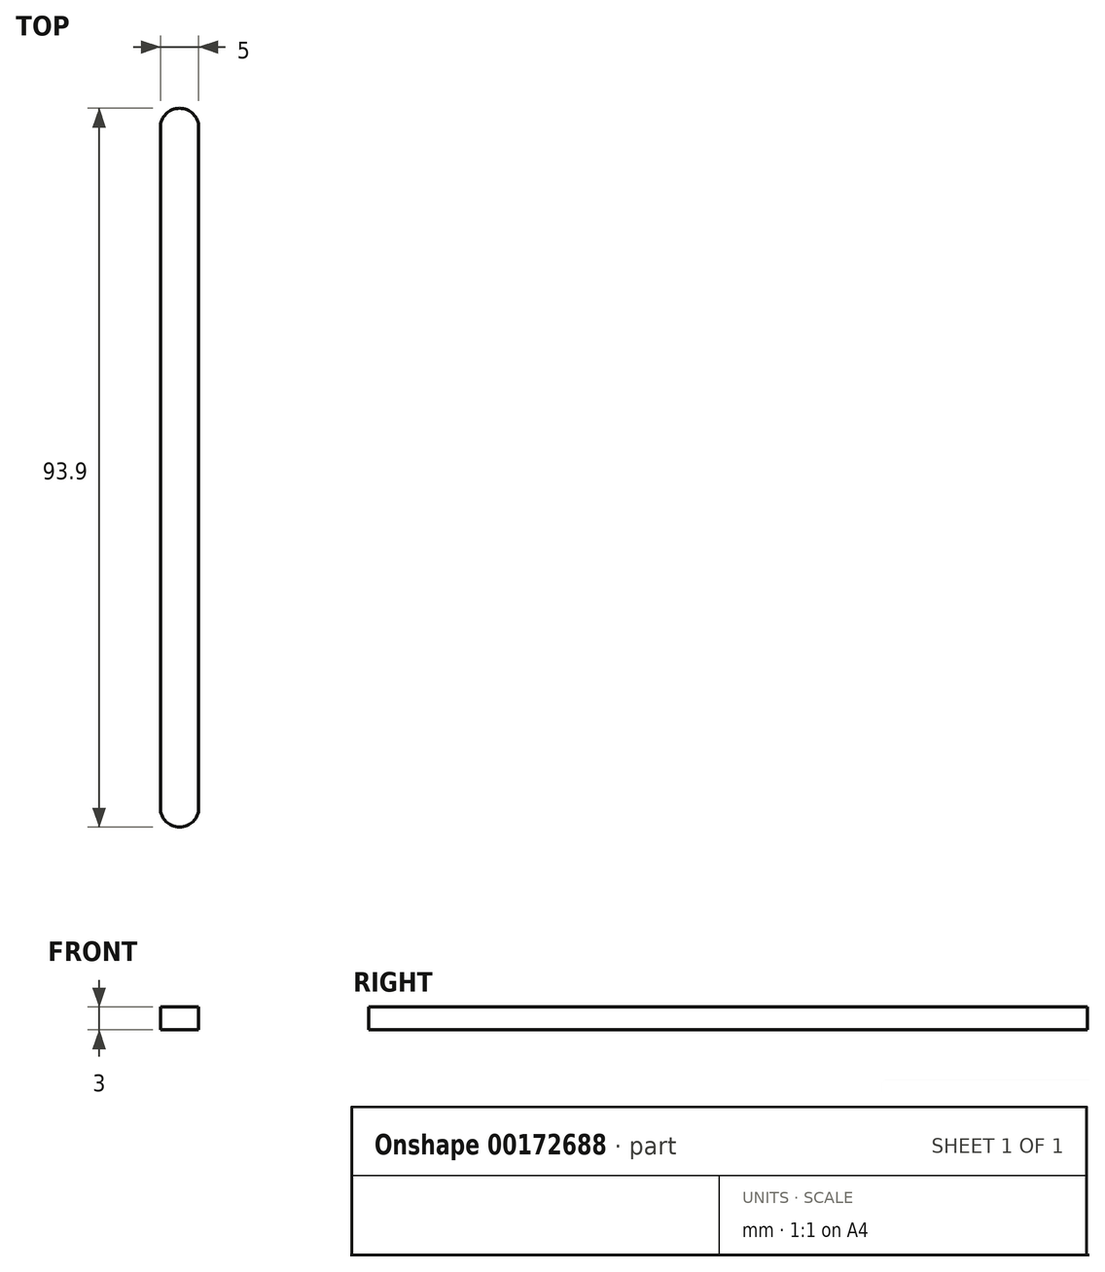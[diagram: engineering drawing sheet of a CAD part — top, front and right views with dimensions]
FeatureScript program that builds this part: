
annotation { "Feature Type Name" : "Feature", "Feature Type Description" : "" }
export const myFeature = defineFeature(function(context is Context, id is Id, definition is map)
    precondition{}
    {
        {
            var Q0;
            Q0=qCreatedBy(makeId("Top.planeOp"),FACE);
            var sketch = newSketch(context, id + "F0", { "sketchPlane" : qUnion([Q0])});
            skLineSegment(sketch, "E0", {"start": v(-1.75, 67.98) * mm, "end": v(-1.75, -46.32) * mm});
            skLineSegment(sketch, "E1", {"start": v(-22.75, 67.98) * mm, "end": v(-22.75, -20.92) * mm});
            skLineSegment(sketch, "E2", {"start": v(-104.51, -51.12) * mm, "end": v(-35.45, -18.92) * mm});
            skLineSegment(sketch, "E3", {"start": v(-91.81, -68.37) * mm, "end": v(-22.75, -36.16) * mm});
            skLineSegment(sketch, "E4", {"start": v(-99.28, -84.88) * mm, "end": v(50.8, -58.42) * mm});
            skArc(sketch, "E5.4.startCap", {"start": v(-25.25, 67.98) * mm, "mid": v(-22.75, 70.48) * mm, "end": v(-20.25, 67.98) * mm});
            skArc(sketch, "E5.4.endCap", {"start": v(-20.25, -20.92) * mm, "mid": v(-22.75, -23.42) * mm, "end": v(-25.25, -20.92) * mm});
            skLineSegment(sketch, "E5.4.left", {"start": v(-20.25, 67.98) * mm, "end": v(-20.25, -20.92) * mm});
            skLineSegment(sketch, "E5.4.right", {"start": v(-25.25, 67.98) * mm, "end": v(-25.25, -20.92) * mm});
            skArc(sketch, "E5.5.startCap", {"start": v(-103.46, -53.39) * mm, "mid": v(-106.78, -52.18) * mm, "end": v(-105.57, -48.85) * mm});
            skArc(sketch, "E5.5.endCap", {"start": v(-36.5, -16.65) * mm, "mid": v(-33.19, -17.86) * mm, "end": v(-34.4, -21.18) * mm});
            skLineSegment(sketch, "E5.5.left", {"start": v(-105.57, -48.85) * mm, "end": v(-36.5, -16.65) * mm});
            skLineSegment(sketch, "E5.5.right", {"start": v(-103.46, -53.39) * mm, "end": v(-34.4, -21.18) * mm});
            skArc(sketch, "E5.6.startCap", {"start": v(-90.76, -70.63) * mm, "mid": v(-94.08, -69.42) * mm, "end": v(-92.87, -66.1) * mm});
            skArc(sketch, "E5.6.endCap", {"start": v(-23.8, -33.9) * mm, "mid": v(-20.49, -35.1) * mm, "end": v(-21.7, -38.43) * mm});
            skLineSegment(sketch, "E5.6.left", {"start": v(-92.87, -66.1) * mm, "end": v(-23.8, -33.9) * mm});
            skLineSegment(sketch, "E5.6.right", {"start": v(-90.76, -70.63) * mm, "end": v(-21.7, -38.43) * mm});
            skArc(sketch, "E5.7.startCap", {"start": v(-98.85, -87.35) * mm, "mid": v(-101.75, -85.32) * mm, "end": v(-99.72, -82.42) * mm});
            skArc(sketch, "E5.7.endCap", {"start": v(50.37, -55.96) * mm, "mid": v(53.26, -57.99) * mm, "end": v(51.23, -60.88) * mm});
            skLineSegment(sketch, "E5.7.left", {"start": v(-99.72, -82.42) * mm, "end": v(50.37, -55.96) * mm});
            skLineSegment(sketch, "E5.7.right", {"start": v(-98.85, -87.35) * mm, "end": v(51.23, -60.88) * mm});
            skLineSegment(sketch, "E6", {"start": v(-25.75, 75.98) * mm, "end": v(84.75, 75.98) * mm});
            skLineSegment(sketch, "E7", {"start": v(86.14, -60.31) * mm, "end": v(-100.85, -93.28) * mm});
            skLineSegment(sketch, "E8", {"start": v(-106.64, -89.23) * mm, "end": v(-113.28, -51.57) * mm});
            skLineSegment(sketch, "E9", {"start": v(-109.71, -44.72) * mm, "end": v(-45.42, -14.74) * mm});
            skLineSegment(sketch, "E10", {"start": v(-30.75, 8.28) * mm, "end": v(-30.75, 70.98) * mm});
            skPoint(sketch, "E11.visualSharp", {"position": v(-30.75, -7.9) * mm});
            skArc(sketch, "E11.filletArc", {"start": v(-45.42, -14.74) * mm, "mid": v(-34.73, -5.36) * mm, "end": v(-30.75, 8.28) * mm});
            skPoint(sketch, "E12.visualSharp", {"position": v(-108.55, -78.4) * mm});
            skPoint(sketch, "E13.visualSharp", {"position": v(-105.77, -94.15) * mm});
            skArc(sketch, "E13.filletArc", {"start": v(-106.64, -89.23) * mm, "mid": v(-104.59, -92.46) * mm, "end": v(-100.85, -93.28) * mm});
            skPoint(sketch, "E14.visualSharp", {"position": v(-30.75, 75.98) * mm});
            skArc(sketch, "E14.filletArc", {"start": v(-25.75, 75.98) * mm, "mid": v(-29.29, 74.51) * mm, "end": v(-30.75, 70.98) * mm});
            skArc(sketch, "E15.0.startCap", {"start": v(-4.25, 67.98) * mm, "mid": v(-1.75, 70.48) * mm, "end": v(0.75, 67.98) * mm});
            skArc(sketch, "E15.0.endCap", {"start": v(0.75, -46.32) * mm, "mid": v(-1.75, -48.82) * mm, "end": v(-4.25, -46.32) * mm});
            skLineSegment(sketch, "E15.0.left", {"start": v(0.75, 67.98) * mm, "end": v(0.75, -46.32) * mm});
            skLineSegment(sketch, "E15.0.right", {"start": v(-4.25, 67.98) * mm, "end": v(-4.25, -46.32) * mm});
            skLineSegment(sketch, "E16.1.0.0", {"start": v(16.75, 67.98) * mm, "end": v(16.75, -46.32) * mm});
            skLineSegment(sketch, "E16.1.0.1", {"start": v(19.25, 67.98) * mm, "end": v(19.25, -46.32) * mm});
            skLineSegment(sketch, "E16.1.0.2", {"start": v(21.75, 67.98) * mm, "end": v(21.75, -46.32) * mm});
            skArc(sketch, "E16.1.0.3", {"start": v(16.75, 67.98) * mm, "mid": v(19.25, 70.48) * mm, "end": v(21.75, 67.98) * mm});
            skArc(sketch, "E16.1.0.4", {"start": v(21.75, -46.32) * mm, "mid": v(19.25, -48.82) * mm, "end": v(16.75, -46.32) * mm});
            skLineSegment(sketch, "E16.2.0.0", {"start": v(37.75, 67.98) * mm, "end": v(37.75, -46.32) * mm});
            skLineSegment(sketch, "E16.2.0.1", {"start": v(40.25, 67.98) * mm, "end": v(40.25, -46.32) * mm});
            skLineSegment(sketch, "E16.2.0.2", {"start": v(42.75, 67.98) * mm, "end": v(42.75, -46.32) * mm});
            skArc(sketch, "E16.2.0.3", {"start": v(37.75, 67.98) * mm, "mid": v(40.25, 70.48) * mm, "end": v(42.75, 67.98) * mm});
            skArc(sketch, "E16.2.0.4", {"start": v(42.75, -46.32) * mm, "mid": v(40.25, -48.82) * mm, "end": v(37.75, -46.32) * mm});
            skLineSegment(sketch, "E16.3.0.0", {"start": v(58.75, 67.98) * mm, "end": v(58.75, -46.32) * mm});
            skLineSegment(sketch, "E16.3.0.1", {"start": v(61.25, 67.98) * mm, "end": v(61.25, -46.32) * mm});
            skLineSegment(sketch, "E16.3.0.2", {"start": v(63.75, 67.98) * mm, "end": v(63.75, -46.32) * mm});
            skArc(sketch, "E16.3.0.3", {"start": v(58.75, 67.98) * mm, "mid": v(61.25, 70.48) * mm, "end": v(63.75, 67.98) * mm});
            skArc(sketch, "E16.3.0.4", {"start": v(63.75, -46.32) * mm, "mid": v(61.25, -48.82) * mm, "end": v(58.75, -46.32) * mm});
            skLineSegment(sketch, "E16.4.0.0", {"start": v(79.75, 67.98) * mm, "end": v(79.75, -46.32) * mm});
            skLineSegment(sketch, "E16.4.0.1", {"start": v(82.25, 67.98) * mm, "end": v(82.25, -46.32) * mm});
            skLineSegment(sketch, "E16.4.0.2", {"start": v(84.75, 67.98) * mm, "end": v(84.75, -46.32) * mm});
            skArc(sketch, "E16.4.0.3", {"start": v(79.75, 67.98) * mm, "mid": v(82.25, 70.48) * mm, "end": v(84.75, 67.98) * mm});
            skArc(sketch, "E16.4.0.4", {"start": v(84.75, -46.32) * mm, "mid": v(82.25, -48.82) * mm, "end": v(79.75, -46.32) * mm});
            skLineSegment(sketch, "E16.direction1", {"start": v(-4.25, -46.32) * mm, "end": v(16.75, -46.32) * mm, "construction": true});
            skLineSegment(sketch, "E17", {"start": v(92.75, -52.43) * mm, "end": v(92.75, 67.98) * mm});
            skArc(sketch, "E18.filletArc", {"start": v(92.75, 67.98) * mm, "mid": v(90.4, 73.63) * mm, "end": v(84.75, 75.98) * mm});
            skPoint(sketch, "E19.visualSharp", {"position": v(92.75, -59.15) * mm});
            skArc(sketch, "E19.filletArc", {"start": v(86.14, -60.31) * mm, "mid": v(90.88, -57.58) * mm, "end": v(92.75, -52.43) * mm});
            skPoint(sketch, "E20.visualSharp", {"position": v(-114.13, -46.78) * mm});
            skArc(sketch, "E20.filletArc", {"start": v(-109.71, -44.72) * mm, "mid": v(-112.66, -47.54) * mm, "end": v(-113.28, -51.57) * mm});
            skSolve(sketch);
        }
        {
            var Q0;
            Q0=makeQuery(id+"F0.imprint","IMPRINT",FACE,{"disambiguationData":[TD([[makeQuery(id+"F0.imprint","IMPRINT",EDGE,{"derivedFrom":sQuery(id+"F0.wireOp",EDGE,"E5.4.startCap")}),1.0]])]});
            extrude(context, id + "F1", {"entities" : qUnion([Q0]), "depth" : 6 * mm});
        }
        {
            var Q0;
            Q0=makeQuery(id+"F1.opExtrude","CAP_FACE",FACE,{"disambiguationData":[OSD([sQuery(id+"F0.wireOp",EDGE,"E5.4.startCap"),sQuery(id+"F0.wireOp",EDGE,"E5.4.endCap"),sQuery(id+"F0.wireOp",EDGE,"E5.4.left"),sQuery(id+"F0.wireOp",EDGE,"E5.4.right"),sQuery(id+"F0.wireOp",EDGE,"E5.5.startCap"),sQuery(id+"F0.wireOp",EDGE,"E5.5.endCap"),sQuery(id+"F0.wireOp",EDGE,"E5.5.left"),sQuery(id+"F0.wireOp",EDGE,"E5.5.right"),sQuery(id+"F0.wireOp",EDGE,"E5.6.startCap"),sQuery(id+"F0.wireOp",EDGE,"E5.6.endCap"),sQuery(id+"F0.wireOp",EDGE,"E5.6.left"),sQuery(id+"F0.wireOp",EDGE,"E5.6.right"),sQuery(id+"F0.wireOp",EDGE,"E5.7.startCap"),sQuery(id+"F0.wireOp",EDGE,"E5.7.endCap"),sQuery(id+"F0.wireOp",EDGE,"E5.7.left"),sQuery(id+"F0.wireOp",EDGE,"E5.7.right"),sQuery(id+"F0.wireOp",EDGE,"E6"),sQuery(id+"F0.wireOp",EDGE,"E7"),sQuery(id+"F0.wireOp",EDGE,"E8"),sQuery(id+"F0.wireOp",EDGE,"ev5cbhRx-Xfhe-EjYM-3IOK-P7PErRR7EIuT"),sQuery(id+"F0.wireOp",EDGE,"4vSNfU6F-C1qH-3bgV-W2vF-ly2UdOvPPW9B"),sQuery(id+"F0.wireOp",EDGE,"E9"),sQuery(id+"F0.wireOp",EDGE,"E10"),sQuery(id+"F0.wireOp",EDGE,"07c6aec0-4847-45df-b5d5-83fb8df157c1.filletArc"),sQuery(id+"F0.wireOp",EDGE,"6f2fbac6-5da2-46ef-aa15-745e75e4c3b5.filletArc"),sQuery(id+"F0.wireOp",EDGE,"E11.filletArc"),sQuery(id+"F0.wireOp",EDGE,"E12.filletArc"),sQuery(id+"F0.wireOp",EDGE,"E13.filletArc"),sQuery(id+"F0.wireOp",EDGE,"E14.filletArc"),sQuery(id+"F0.wireOp",EDGE,"E15.0.startCap"),sQuery(id+"F0.wireOp",EDGE,"E15.0.endCap"),sQuery(id+"F0.wireOp",EDGE,"E15.0.left"),sQuery(id+"F0.wireOp",EDGE,"E15.0.right"),sQuery(id+"F0.wireOp",EDGE,"E16.1.0.0"),sQuery(id+"F0.wireOp",EDGE,"E16.1.0.2"),sQuery(id+"F0.wireOp",EDGE,"E16.1.0.3"),sQuery(id+"F0.wireOp",EDGE,"E16.1.0.4"),sQuery(id+"F0.wireOp",EDGE,"E16.2.0.0"),sQuery(id+"F0.wireOp",EDGE,"E16.2.0.2"),sQuery(id+"F0.wireOp",EDGE,"E16.2.0.3"),sQuery(id+"F0.wireOp",EDGE,"E16.2.0.4"),sQuery(id+"F0.wireOp",EDGE,"E16.3.0.0"),sQuery(id+"F0.wireOp",EDGE,"E16.3.0.2"),sQuery(id+"F0.wireOp",EDGE,"E16.3.0.3"),sQuery(id+"F0.wireOp",EDGE,"E16.3.0.4"),sQuery(id+"F0.wireOp",EDGE,"E16.4.0.0"),sQuery(id+"F0.wireOp",EDGE,"E16.4.0.2"),sQuery(id+"F0.wireOp",EDGE,"E16.4.0.3"),sQuery(id+"F0.wireOp",EDGE,"E16.4.0.4"),sQuery(id+"F0.wireOp",EDGE,"E17"),sQuery(id+"F0.wireOp",EDGE,"E18.filletArc"),sQuery(id+"F0.wireOp",EDGE,"E19.filletArc")])],"isStart":true});
            var sketch = newSketch(context, id + "F2", { "sketchPlane" : qUnion([Q0])});
            skLineSegment(sketch, "E21", {"start": v(82.25, 46.32) * mm, "end": v(82.25, -67.98) * mm});
            skLineSegment(sketch, "E22", {"start": v(61.25, 46.32) * mm, "end": v(61.25, -67.98) * mm});
            skLineSegment(sketch, "E23", {"start": v(40.25, 46.32) * mm, "end": v(40.25, -67.98) * mm});
            skLineSegment(sketch, "E24", {"start": v(19.25, 46.32) * mm, "end": v(19.25, -67.98) * mm});
            skLineSegment(sketch, "E25", {"start": v(-1.75, 46.32) * mm, "end": v(-1.75, -67.98) * mm});
            skLineSegment(sketch, "E26", {"start": v(-22.75, 20.92) * mm, "end": v(-22.75, -67.98) * mm});
            skLineSegment(sketch, "E27", {"start": v(-35.45, 18.92) * mm, "end": v(-104.51, 51.12) * mm});
            skLineSegment(sketch, "E28", {"start": v(-22.75, 36.16) * mm, "end": v(-91.81, 68.37) * mm});
            skLineSegment(sketch, "E29", {"start": v(50.8, 58.42) * mm, "end": v(-99.28, 84.88) * mm});
            skArc(sketch, "E30.0.startCap", {"start": v(77.25, 46.32) * mm, "mid": v(82.25, 51.32) * mm, "end": v(87.25, 46.32) * mm});
            skArc(sketch, "E30.0.endCap", {"start": v(87.25, -67.98) * mm, "mid": v(82.25, -72.98) * mm, "end": v(77.25, -67.98) * mm});
            skLineSegment(sketch, "E30.0.left", {"start": v(87.25, 46.32) * mm, "end": v(87.25, -67.98) * mm});
            skLineSegment(sketch, "E30.0.right", {"start": v(77.25, 46.32) * mm, "end": v(77.25, -67.98) * mm});
            skArc(sketch, "E30.1.startCap", {"start": v(56.25, 46.32) * mm, "mid": v(61.25, 51.32) * mm, "end": v(66.25, 46.32) * mm});
            skArc(sketch, "E30.1.endCap", {"start": v(66.25, -67.98) * mm, "mid": v(61.25, -72.98) * mm, "end": v(56.25, -67.98) * mm});
            skLineSegment(sketch, "E30.1.left", {"start": v(66.25, 46.32) * mm, "end": v(66.25, -67.98) * mm});
            skLineSegment(sketch, "E30.1.right", {"start": v(56.25, 46.32) * mm, "end": v(56.25, -67.98) * mm});
            skArc(sketch, "E30.2.startCap", {"start": v(35.25, 46.32) * mm, "mid": v(40.25, 51.32) * mm, "end": v(45.25, 46.32) * mm});
            skArc(sketch, "E30.2.endCap", {"start": v(45.25, -67.98) * mm, "mid": v(40.25, -72.98) * mm, "end": v(35.25, -67.98) * mm});
            skLineSegment(sketch, "E30.2.left", {"start": v(45.25, 46.32) * mm, "end": v(45.25, -67.98) * mm});
            skLineSegment(sketch, "E30.2.right", {"start": v(35.25, 46.32) * mm, "end": v(35.25, -67.98) * mm});
            skArc(sketch, "E30.3.startCap", {"start": v(14.25, 46.32) * mm, "mid": v(19.25, 51.32) * mm, "end": v(24.25, 46.32) * mm});
            skArc(sketch, "E30.3.endCap", {"start": v(24.25, -67.98) * mm, "mid": v(19.25, -72.98) * mm, "end": v(14.25, -67.98) * mm});
            skLineSegment(sketch, "E30.3.left", {"start": v(24.25, 46.32) * mm, "end": v(24.25, -67.98) * mm});
            skLineSegment(sketch, "E30.3.right", {"start": v(14.25, 46.32) * mm, "end": v(14.25, -67.98) * mm});
            skArc(sketch, "E30.4.startCap", {"start": v(-6.75, 46.32) * mm, "mid": v(-1.75, 51.32) * mm, "end": v(3.25, 46.32) * mm});
            skArc(sketch, "E30.4.endCap", {"start": v(3.25, -67.98) * mm, "mid": v(-1.75, -72.98) * mm, "end": v(-6.75, -67.98) * mm});
            skLineSegment(sketch, "E30.4.left", {"start": v(3.25, 46.32) * mm, "end": v(3.25, -67.98) * mm});
            skLineSegment(sketch, "E30.4.right", {"start": v(-6.75, 46.32) * mm, "end": v(-6.75, -67.98) * mm});
            skArc(sketch, "E30.5.startCap", {"start": v(-20.64, 40.7) * mm, "mid": v(-18.22, 34.05) * mm, "end": v(-24.86, 31.63) * mm});
            skArc(sketch, "E30.5.endCap", {"start": v(-93.92, 63.84) * mm, "mid": v(-96.34, 70.48) * mm, "end": v(-89.7, 72.9) * mm});
            skLineSegment(sketch, "E30.5.left", {"start": v(-24.86, 31.63) * mm, "end": v(-93.92, 63.84) * mm});
            skLineSegment(sketch, "E30.5.right", {"start": v(-20.64, 40.7) * mm, "end": v(-89.7, 72.9) * mm});
            skArc(sketch, "E30.6.startCap", {"start": v(-27.75, 20.92) * mm, "mid": v(-22.75, 25.92) * mm, "end": v(-17.75, 20.92) * mm});
            skArc(sketch, "E30.6.endCap", {"start": v(-17.75, -67.98) * mm, "mid": v(-22.75, -72.98) * mm, "end": v(-27.75, -67.98) * mm});
            skLineSegment(sketch, "E30.6.left", {"start": v(-17.75, 20.92) * mm, "end": v(-17.75, -67.98) * mm});
            skLineSegment(sketch, "E30.6.right", {"start": v(-27.75, 20.92) * mm, "end": v(-27.75, -67.98) * mm});
            skArc(sketch, "E30.7.startCap", {"start": v(-33.34, 23.45) * mm, "mid": v(-30.92, 16.8) * mm, "end": v(-37.56, 14.38) * mm});
            skArc(sketch, "E30.7.endCap", {"start": v(-106.62, 46.59) * mm, "mid": v(-109.04, 53.23) * mm, "end": v(-102.4, 55.65) * mm});
            skLineSegment(sketch, "E30.7.left", {"start": v(-37.56, 14.38) * mm, "end": v(-106.62, 46.59) * mm});
            skLineSegment(sketch, "E30.7.right", {"start": v(-33.34, 23.45) * mm, "end": v(-102.4, 55.65) * mm});
            skArc(sketch, "E30.8.startCap", {"start": v(51.67, 63.34) * mm, "mid": v(55.72, 57.55) * mm, "end": v(49.93, 53.5) * mm});
            skArc(sketch, "E30.8.endCap", {"start": v(-100.15, 79.96) * mm, "mid": v(-104.2, 85.75) * mm, "end": v(-98.42, 89.8) * mm});
            skLineSegment(sketch, "E30.8.left", {"start": v(49.93, 53.5) * mm, "end": v(-100.15, 79.96) * mm});
            skLineSegment(sketch, "E30.8.right", {"start": v(51.67, 63.34) * mm, "end": v(-98.42, 89.8) * mm});
            skSolve(sketch);
        }
        {
            var Q0;
            Q0 = qSketchRegion(id + "F2", true);
            extrude(context, id + "F3", {"entities" : qUnion([Q0]), "operationType" : NewBodyOperationType.REMOVE, "oppositeDirection" : true, "depth" : 3 * mm});
        }
    });
